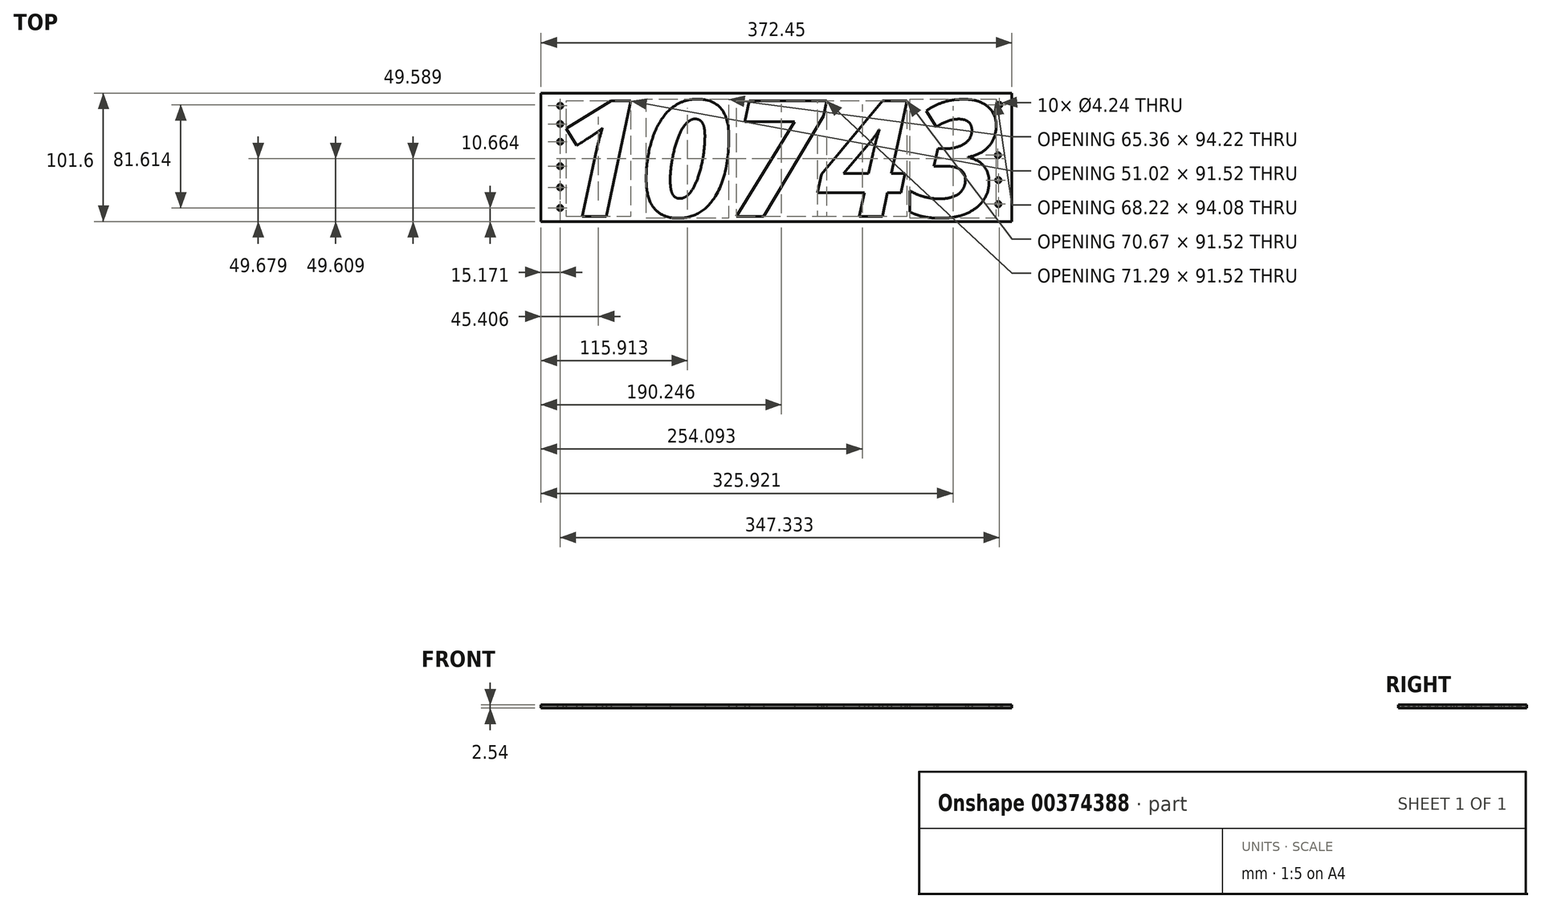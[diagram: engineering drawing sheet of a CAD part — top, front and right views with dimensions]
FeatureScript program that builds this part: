
annotation { "Feature Type Name" : "Feature", "Feature Type Description" : "" }
export const myFeature = defineFeature(function(context is Context, id is Id, definition is map)
    precondition{}
    {
        {
            var Q0;
            Q0=qCreatedBy(makeId("Top.planeOp"),FACE);
            var sketch = newSketch(context, id + "F0", { "sketchPlane" : qUnion([Q0])});
            skLineSegment(sketch, "E0.bottom", {"start": v(-179.17, 39.73) * mm, "end": v(184.3, 39.73) * mm});
            skLineSegment(sketch, "E0.top", {"start": v(-179.17, -52.58) * mm, "end": v(184.3, -52.58) * mm});
            skLineSegment(sketch, "E0.left", {"start": v(-179.17, 39.73) * mm, "end": v(-179.17, -52.58) * mm});
            skLineSegment(sketch, "E0.right", {"start": v(184.3, 39.73) * mm, "end": v(184.3, -52.58) * mm});
            skText(sketch, "E1", { "text": "10743", "fontName": "OpenSans-BoldItalic.ttf"});
            skLineSegment(sketch, "E2.bottom", {"start": v(-188.44, 45.19) * mm, "end": v(184.01, 45.19) * mm});
            skLineSegment(sketch, "E2.top", {"start": v(-188.44, -56.41) * mm, "end": v(184.01, -56.41) * mm});
            skLineSegment(sketch, "E2.left", {"start": v(-188.44, 45.19) * mm, "end": v(-188.44, -56.41) * mm});
            skLineSegment(sketch, "E2.right", {"start": v(184.01, 45.19) * mm, "end": v(184.01, -56.41) * mm});
            skCircle(sketch, "E3", {"center": v(-173.27, 35.1) * mm, "radius": 2.12 * mm});
            skCircle(sketch, "E4", {"center": v(-173.27, -45.75) * mm, "radius": 2.12 * mm});
            skCircle(sketch, "E5", {"center": v(-173.27, -12.72) * mm, "radius": 2.12 * mm});
            skCircle(sketch, "E6", {"center": v(-173.27, 6.64) * mm, "radius": 2.12 * mm});
            skCircle(sketch, "E7", {"center": v(-173.27, 20.68) * mm, "radius": 2.12 * mm});
            skCircle(sketch, "E8", {"center": v(-173.27, -29.42) * mm, "radius": 2.12 * mm});
            skCircle(sketch, "E9", {"center": v(174.06, 35.87) * mm, "radius": 2.12 * mm});
            skCircle(sketch, "E10", {"center": v(173.3, -42.7) * mm, "radius": 2.12 * mm});
            skCircle(sketch, "E11", {"center": v(173.3, -23.73) * mm, "radius": 2.12 * mm});
            skCircle(sketch, "E12", {"center": v(172.93, -3.99) * mm, "radius": 2.12 * mm});
            const initialGuessF0  = {"E1": [-0.17994, -0.05258, 1, 0, 0.0923]};
            skSetInitialGuess(sketch, initialGuessF0);
            skSolve(sketch);
        }
        {
            var Q0;
            {var subQ16=sQuery(id+"F0.wireOp",EDGE,"E1.sketch_text.stroke-9");Q0=makeQuery(id+"F0.imprint","IMPRINT",FACE,{"disambiguationData":[TD([[makeQuery(id+"F0.imprint","IMPRINT",EDGE,{"derivedFrom":subQ16}),1.0]])]});}
            var Q1;
            {var subQ22=sQuery(id+"F0.wireOp",EDGE,"E0.left");Q1=makeQuery(id+"F0.imprint","IMPRINT",FACE,{"disambiguationData":[TD([[makeQuery(id+"F0.imprint","IMPRINT",EDGE,{"derivedFrom":subQ22}),-1.0]])]});}
            var Q2;
            Q2=makeQuery(id+"F0.imprint","IMPRINT",FACE,{"disambiguationData":[TD([[makeQuery(id+"F0.imprint","IMPRINT",EDGE,{"derivedFrom":sQuery(id+"F0.wireOp",EDGE,"E1.sketch_text.stroke-17")}),1.0]])]});
            var Q3;
            Q3=makeQuery(id+"F0.imprint","IMPRINT",FACE,{"disambiguationData":[TD([[makeQuery(id+"F0.imprint","IMPRINT",EDGE,{"derivedFrom":sQuery(id+"F0.wireOp",EDGE,"E1.sketch_text.stroke-45")}),1.0]])]});
            var Q4;
            {var subQ11=sQuery(id+"F0.wireOp",EDGE,"E0.left");Q4=makeQuery(id+"F0.imprint","IMPRINT",FACE,{"disambiguationData":[TD([[makeQuery(id+"F0.imprint","IMPRINT",EDGE,{"derivedFrom":subQ11}),1.0]])]});}
            var Q5;
            Q5=makeQuery(id+"F0.imprint","IMPRINT",FACE,{"disambiguationData":[TD([[makeQuery(id+"F0.imprint","IMPRINT",EDGE,{"derivedFrom":sQuery(id+"F0.wireOp",EDGE,"E1.sketch_text.stroke-52")}),1.0]])]});
            extrude(context, id + "F1", {"entities" : qUnion([Q0, Q1, Q2, Q3, Q4, Q5]), "depth" : 2.54 * mm});
        }
    });
